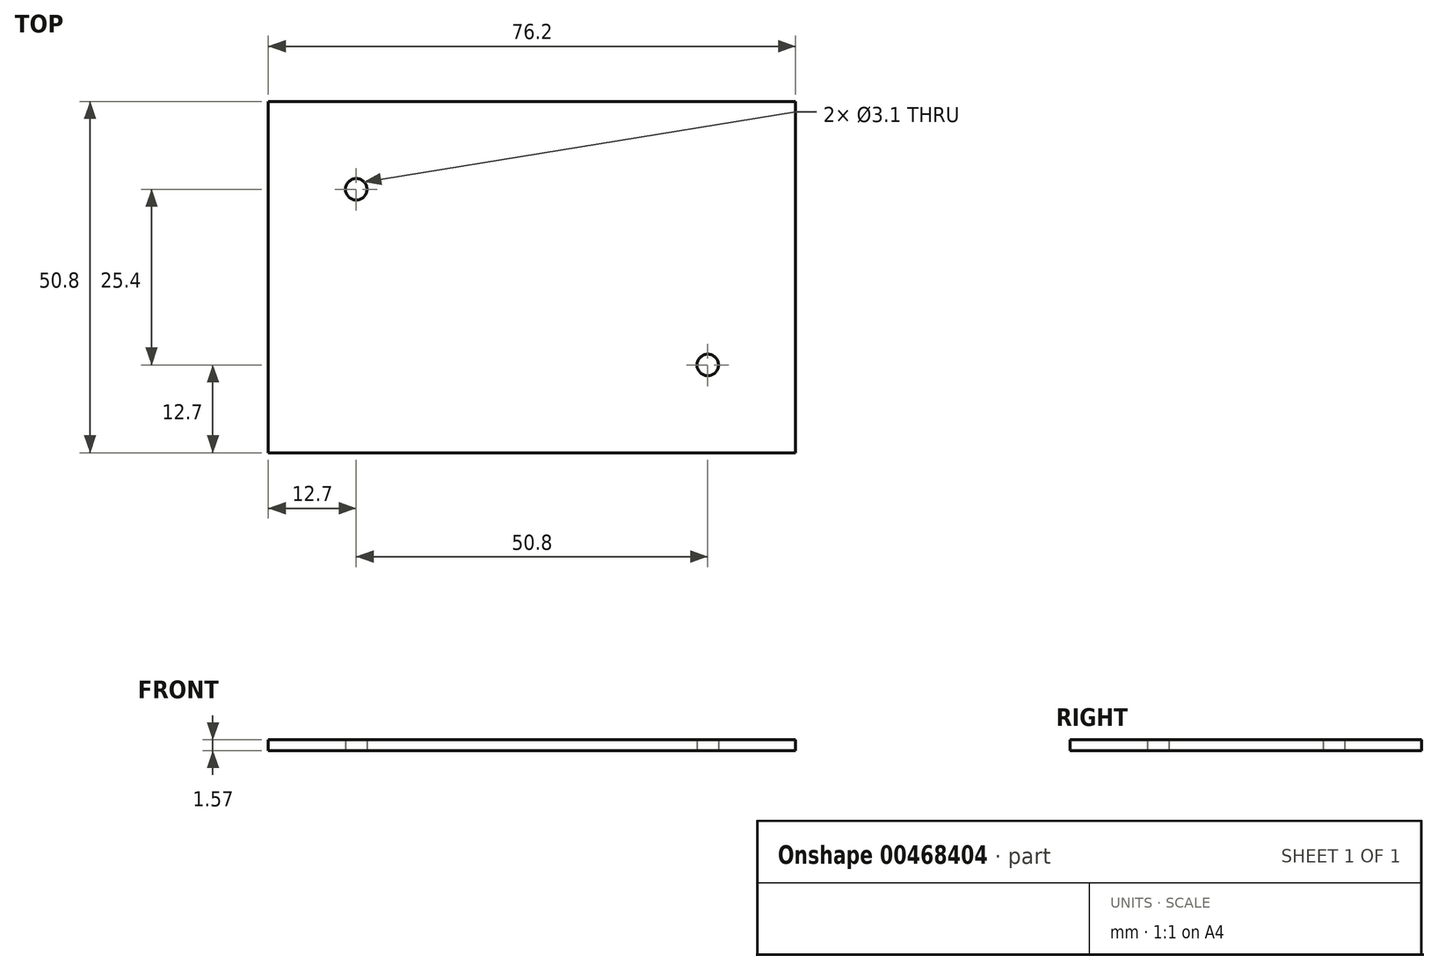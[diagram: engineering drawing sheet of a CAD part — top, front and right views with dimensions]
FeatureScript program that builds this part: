
annotation { "Feature Type Name" : "Feature", "Feature Type Description" : "" }
export const myFeature = defineFeature(function(context is Context, id is Id, definition is map)
    precondition{}
    {
        {
            var Q0;
            Q0=qCreatedBy(makeId("Top.planeOp"),FACE);
            var sketch = newSketch(context, id + "F0", { "sketchPlane" : qUnion([Q0])});
            skLineSegment(sketch, "E0.bottom", {"start": v(38.1, -25.4) * mm, "end": v(-38.1, -25.4) * mm});
            skLineSegment(sketch, "E0.top", {"start": v(38.1, 25.4) * mm, "end": v(-38.1, 25.4) * mm});
            skLineSegment(sketch, "E0.left", {"start": v(38.1, -25.4) * mm, "end": v(38.1, 25.4) * mm});
            skLineSegment(sketch, "E0.right", {"start": v(-38.1, -25.4) * mm, "end": v(-38.1, 25.4) * mm});
            skPoint(sketch, "E0.middle", {"position": v(0, 0) * mm});
            skCircle(sketch, "E1", {"center": v(-25.4, 12.7) * mm, "radius": 1.55 * mm});
            skCircle(sketch, "E2", {"center": v(25.4, -12.7) * mm, "radius": 1.55 * mm});
            skSolve(sketch);
        }
        {
            var Q0;
            Q0 = qSketchRegion(id + "F0", true);
            extrude(context, id + "F1", {"entities" : qUnion([Q0]), "depth" : 1.57 * mm});
        }
    });
